# Revit family: 14309 Столик «Параллель» Хоббика
name_source: partatom
category: Антураж
revit_build: Autodesk Revit 2018 (Build: 20180423_1000(x64)
units: mm (PartAtom-declared; Revit-internal decimal feet)

## family parameters
Всегда вертикально = Да
Источник визуального образа = Геометрия семейства
На основе рабочей плоскости = Нет
Общий = Нет
При загрузке вырезать с полостями = Нет
Точка расчета площади = Нет

## types (2) — shared parameters
URL = https://hobbyka.ru
Артикул товара = Арт. 14309
Высота = 390 мм
Группа модели = Мебель для дома и террас
Длина = 700 мм
Изготовитель = ООО «Хоббика»
Изображение типоразмера = Столик «Параллель» со стеклянной столешницей Арт 14309.jpg
Цвет каркаса = Сталь
Цвет отделки = Дерево
Цвет стекла = Стекло
Ширина = 700 мм

## per-type parameters (varying)
| type | Деревянная столешница | Материал изделия | Описание | Стеклянная столешница |
| Деревянная столешница | Да | Сталь, дерево | Столик «Параллель» с деревянной столешницей | Нет |
| Стеклянная столешница | Нет | Сталь, дерево, стекло | Столик «Параллель» со стеклянной столешницей | Да |
